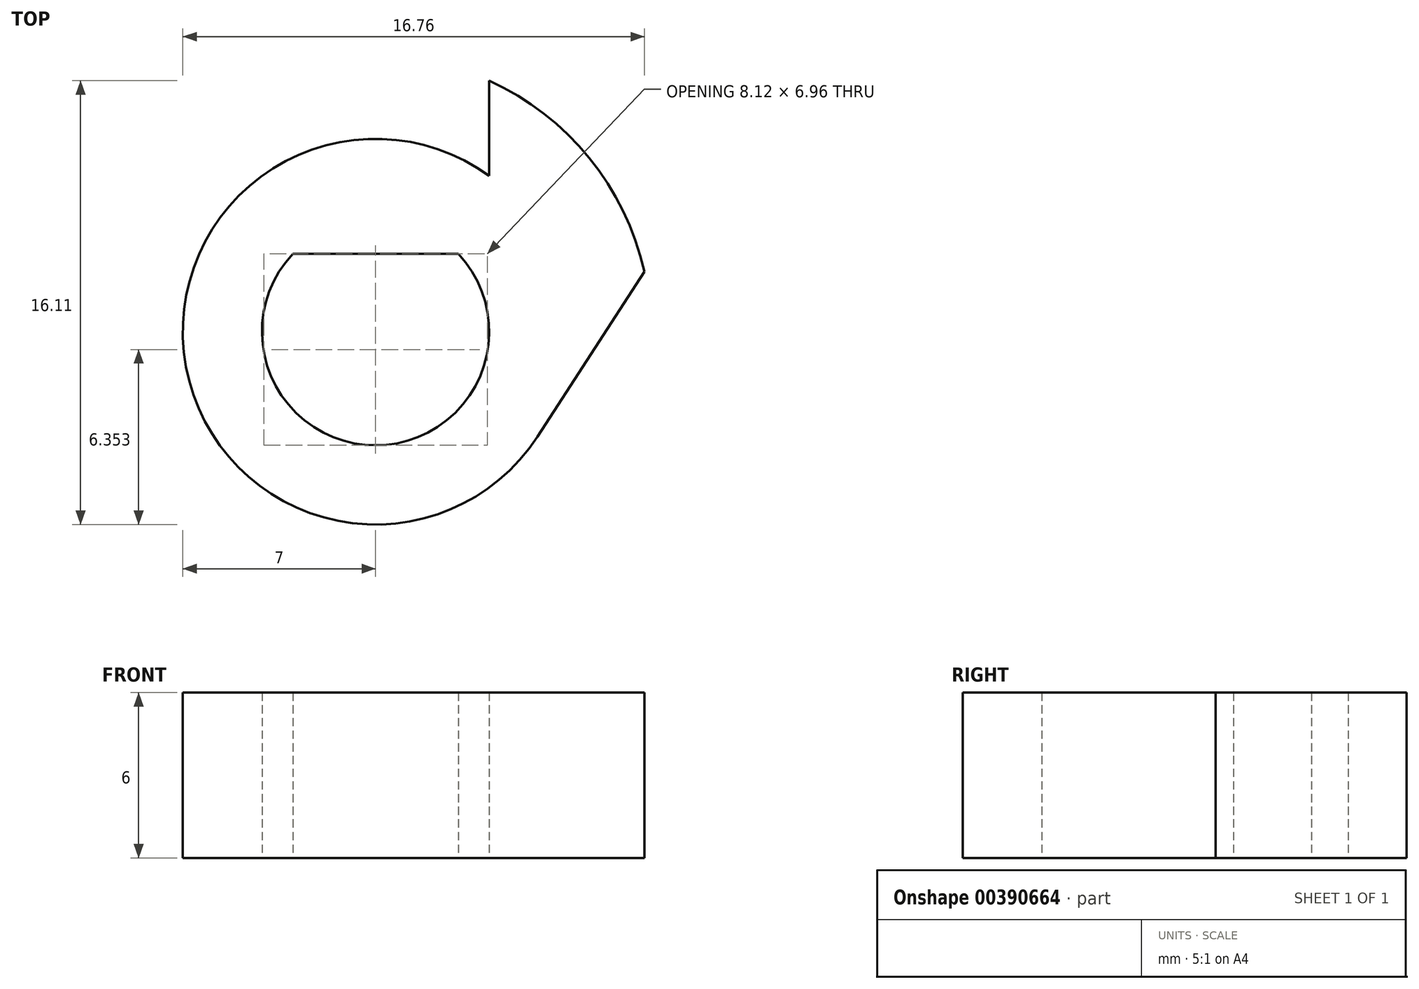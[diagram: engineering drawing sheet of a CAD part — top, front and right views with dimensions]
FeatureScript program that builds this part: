
annotation { "Feature Type Name" : "Feature", "Feature Type Description" : "" }
export const myFeature = defineFeature(function(context is Context, id is Id, definition is map)
    precondition{}
    {
        {
            var Q0;
            Q0=qCreatedBy(makeId("Top.planeOp"),FACE);
            var sketch = newSketch(context, id + "F0", { "sketchPlane" : qUnion([Q0])});
            skCircle(sketch, "E0", {"center": v(0, 0) * mm, "radius": 4.12 * mm});
            skLineSegment(sketch, "E1", {"start": v(-3, 2.83) * mm, "end": v(3, 2.83) * mm});
            skCircle(sketch, "E2", {"center": v(0, 0) * mm, "radius": 10 * mm});
            skCircle(sketch, "E3", {"center": v(0, 0) * mm, "radius": 7 * mm});
            skLineSegment(sketch, "E4", {"start": v(-4.12, 0) * mm, "end": v(-4.12, 9.1) * mm, "construction": true});
            skLineSegment(sketch, "E5", {"start": v(4.12, 0) * mm, "end": v(4.12, 9.1) * mm, "construction": true});
            skLineSegment(sketch, "E6", {"start": v(-4.12, 5.66) * mm, "end": v(-4.12, 9.1) * mm});
            skLineSegment(sketch, "E7", {"start": v(4.12, 5.66) * mm, "end": v(4.12, 9.1) * mm});
            skLineSegment(sketch, "E8", {"start": v(5.87, -3.8) * mm, "end": v(9.76, 2.18) * mm});
            skSolve(sketch);
        }
        {
            var Q0;
            {var subQ0=sQuery(id+"F0.wireOp",EDGE,"E1");var subQ1=sQuery(id+"F0.wireOp",EDGE,"E0");var subQ2=makeQuery(id+"F0.imprint","INTERSECT",VERTEX,{"disambiguationData":[OD(0.0)],"derivedFrom":[subQ1,subQ0]});Q0=makeQuery(id+"F0.imprint","IMPRINT",FACE,{"disambiguationData":[TD([[makeQuery(id+"F0.imprint","IMPRINT",EDGE,{"disambiguationData":[TD([[subQ2,1.0]])],"derivedFrom":subQ1}),-1.0]])]});}
            var Q1;
            {var subQ0=sQuery(id+"F0.wireOp",EDGE,"E1");Q1=makeQuery(id+"F0.imprint","IMPRINT",FACE,{"disambiguationData":[TD([[makeQuery(id+"F0.imprint","IMPRINT",EDGE,{"derivedFrom":subQ0}),1.0]])]});}
            var Q2;
            {var subQ0=sQuery(id+"F0.wireOp",EDGE,"E7");Q2=makeQuery(id+"F0.imprint","IMPRINT",FACE,{"disambiguationData":[TD([[makeQuery(id+"F0.imprint","IMPRINT",EDGE,{"derivedFrom":subQ0}),-1.0]])]});}
            extrude(context, id + "F1", {"entities" : qUnion([Q0, Q1, Q2]), "offsetDistance" : 25 * mm, "depth" : 6 * mm});
        }
    });
